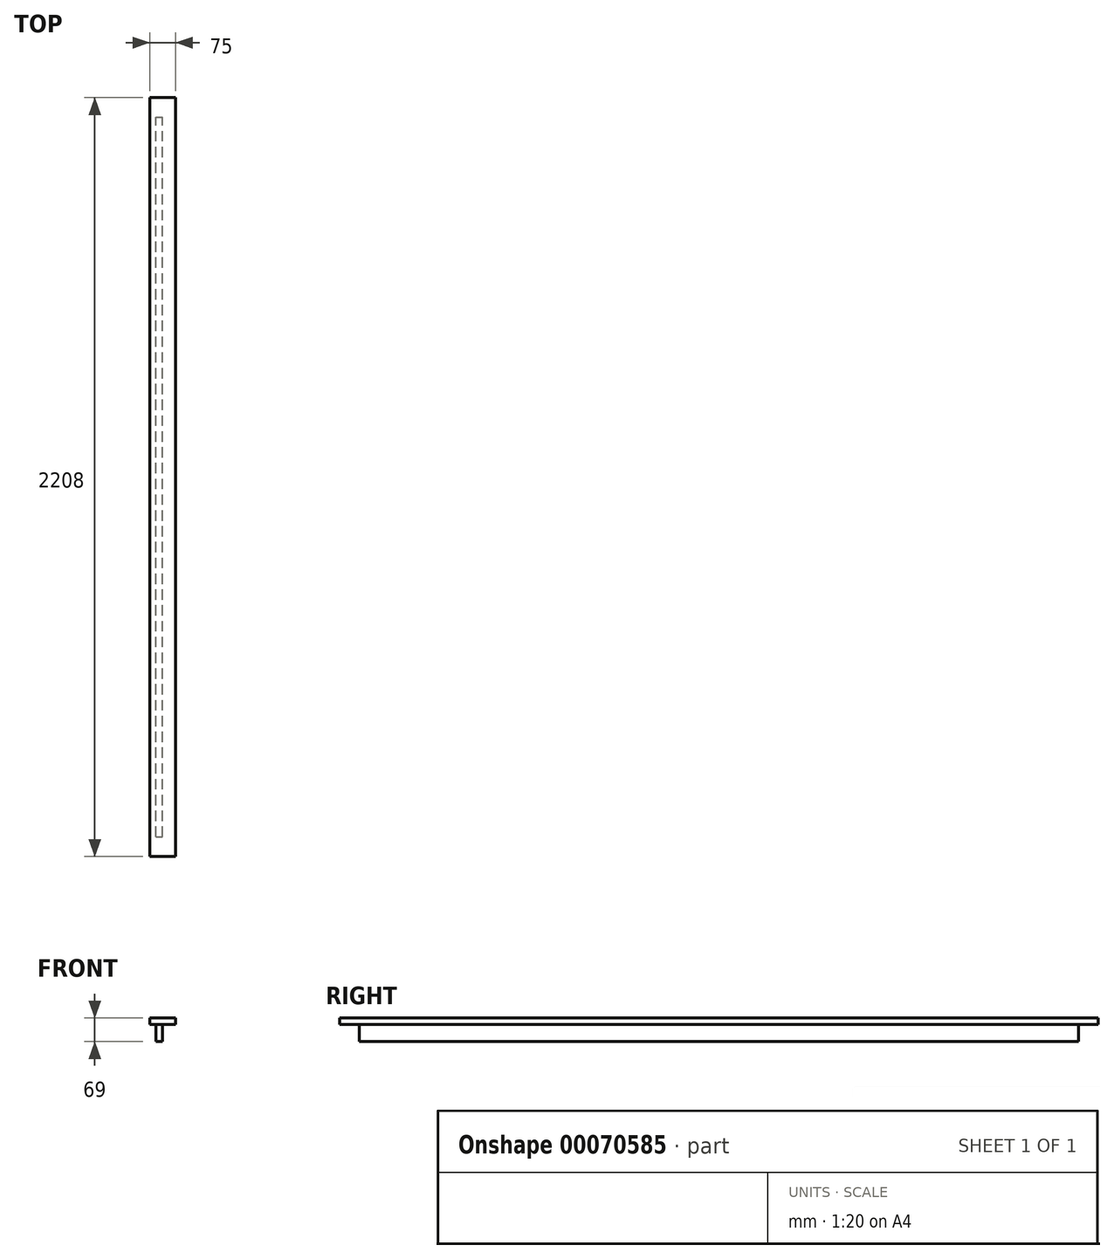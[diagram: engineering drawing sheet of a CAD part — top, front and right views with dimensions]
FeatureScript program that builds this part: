
annotation { "Feature Type Name" : "Feature", "Feature Type Description" : "" }
export const myFeature = defineFeature(function(context is Context, id is Id, definition is map)
    precondition{}
    {
        {
            var Q0;
            Q0=qCreatedBy(makeId("Front.planeOp"),FACE);
            var sketch = newSketch(context, id + "F0", { "sketchPlane" : qUnion([Q0])});
            skLineSegment(sketch, "E0", {"start": v(0, 0) * mm, "end": v(-75, 0) * mm});
            skLineSegment(sketch, "E1", {"start": v(-75, 0) * mm, "end": v(-75, -19) * mm});
            skLineSegment(sketch, "E2", {"start": v(-75, -19) * mm, "end": v(0, -19) * mm});
            skLineSegment(sketch, "E3", {"start": v(0, -19) * mm, "end": v(0, 0) * mm});
            skSolve(sketch);
        }
        {
            var Q0;
            Q0=qSketchRegion(id+"F0",true);
            extrude(context, id + "F1", {"entities" : qUnion([Q0]), "endBound" : BoundingType.SYMMETRIC, "depth" : 2208 * mm});
        }
        {
            var Q0;
            Q0=makeQuery(id+"F1.opExtrude","SWEPT_FACE",FACE,{"disambiguationData":[OSD([sQuery(id+"F0.wireOp",EDGE,"E2")])]});
            var sketch = newSketch(context, id + "F2", { "sketchPlane" : qUnion([Q0])});
            skLineSegment(sketch, "E4.bottom", {"start": v(-57, 1047) * mm, "end": v(-38, 1047) * mm});
            skLineSegment(sketch, "E4.top", {"start": v(-57, -1047) * mm, "end": v(-38, -1047) * mm});
            skLineSegment(sketch, "E4.left", {"start": v(-57, 1047) * mm, "end": v(-57, -1047) * mm});
            skLineSegment(sketch, "E4.right", {"start": v(-38, 1047) * mm, "end": v(-38, -1047) * mm});
            skSolve(sketch);
        }
        {
            var Q0;
            Q0 = qSketchRegion(id + "F2", true);
            extrude(context, id + "F3", {"entities" : qUnion([Q0]), "operationType" : NewBodyOperationType.ADD, "depth" : 50 * mm});
        }
    });
